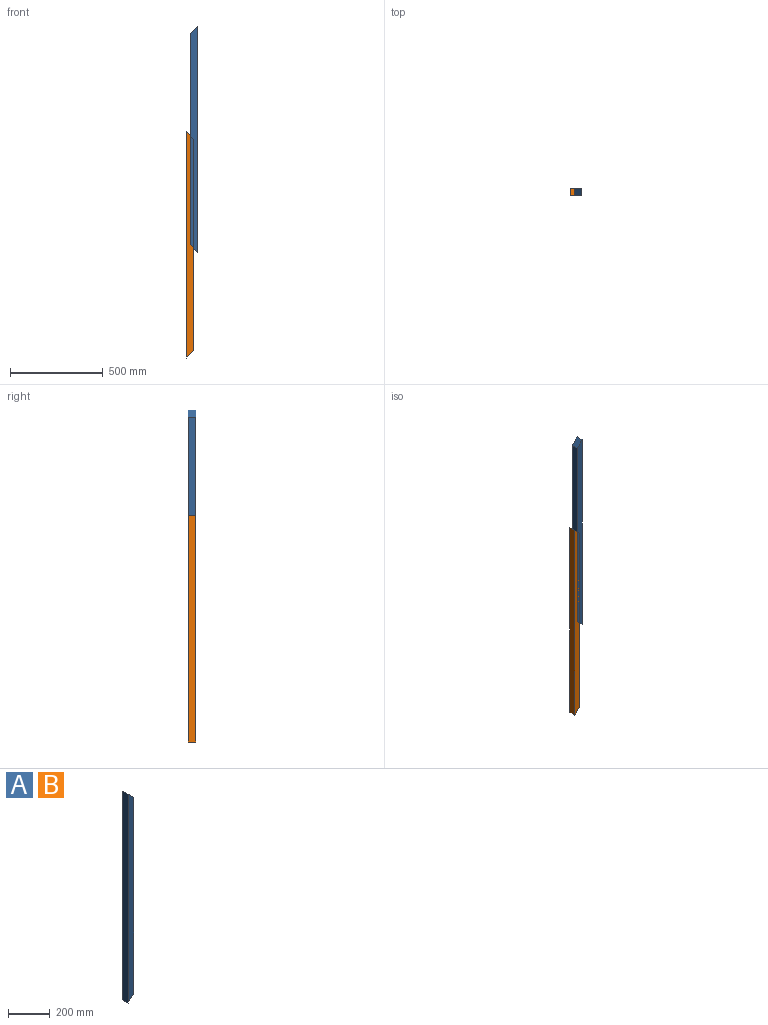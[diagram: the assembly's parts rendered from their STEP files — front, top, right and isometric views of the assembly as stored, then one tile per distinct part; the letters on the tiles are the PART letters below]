
ASSEMBLY  parts=2 mates=1
PART A: 6 faces, bbox 38.1x38.1x1219.2 mm
  f0: plane 1143x38.1mm, normal (1,0,0), area 43548.3mm2, adj f2,f3,f4,f5
  f1: plane 1219.2x38.1mm, normal (-1,0,0), area 46451.5mm2, adj f2,f3,f4,f5
  f2: plane 1219.2x38.1mm, normal (0,-1,0), area 44999.9mm2, adj f0,f1,f4,f5
  f3: plane 1219.2x38.1mm, normal (0,1,0), area 44999.9mm2, adj f0,f1,f4,f5
  f4: plane 38.1x38.1mm, normal (0.71,0,-0.71), area 2052.9mm2, adj f0,f1,f2,f3
  f5: plane 38.1x38.1mm, normal (0.71,0,0.71), area 2052.9mm2, adj f0,f1,f2,f3
PART B: same geometry as A
PLACE A rot(axis=(0,0,1),180deg) t=(-179.67,44.96,243.48)mm
PLACE B t=(-236.61,83.06,-328.02)mm fixed
MATE fastened B.f2 <-> A.f3  axis (0,-1,0) through (-217.77,44.96,281.58)mm
